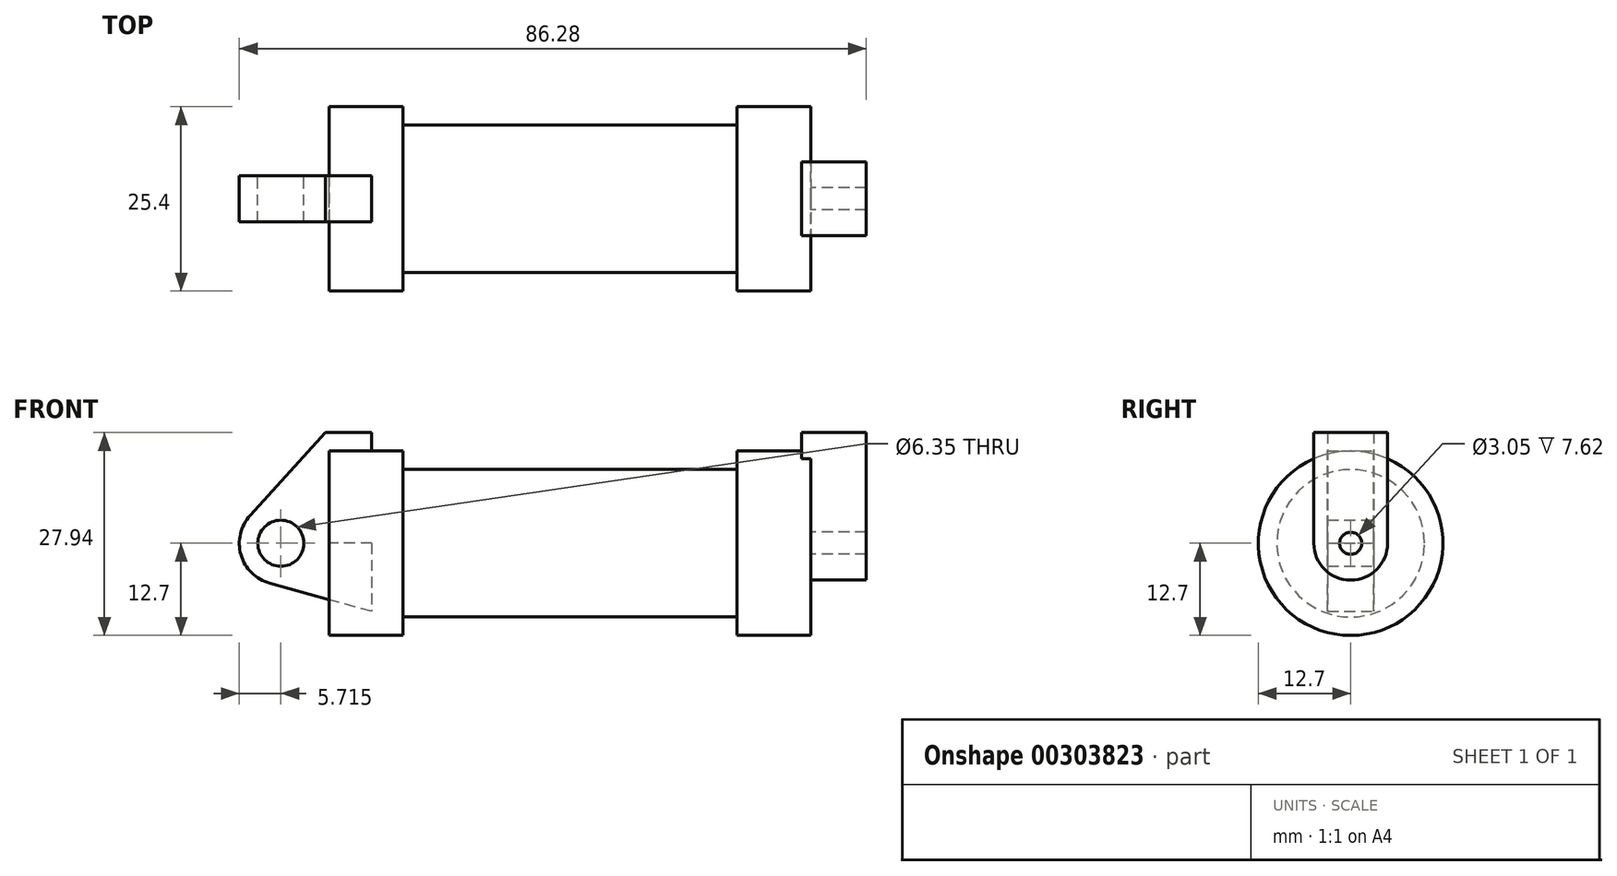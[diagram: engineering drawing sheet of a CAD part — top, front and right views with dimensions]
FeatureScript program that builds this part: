
annotation { "Feature Type Name" : "Feature", "Feature Type Description" : "" }
export const myFeature = defineFeature(function(context is Context, id is Id, definition is map)
    precondition{}
    {
        {
            var Q0;
            Q0=qCreatedBy(makeId("Front.planeOp"),FACE);
            var sketch = newSketch(context, id + "F0", { "sketchPlane" : qUnion([Q0])});
            skLineSegment(sketch, "E0", {"start": v(0, 0) * mm, "end": v(0, 12.7) * mm});
            skLineSegment(sketch, "E1", {"start": v(0, 12.7) * mm, "end": v(10.16, 12.7) * mm});
            skLineSegment(sketch, "E2", {"start": v(10.16, 12.7) * mm, "end": v(10.16, 10.16) * mm});
            skLineSegment(sketch, "E3", {"start": v(10.16, 10.16) * mm, "end": v(56.13, 10.16) * mm});
            skLineSegment(sketch, "E4", {"start": v(56.13, 10.16) * mm, "end": v(56.13, 12.7) * mm});
            skLineSegment(sketch, "E5", {"start": v(56.13, 12.7) * mm, "end": v(66.3, 12.7) * mm});
            skLineSegment(sketch, "E6", {"start": v(66.3, 12.7) * mm, "end": v(66.3, 0) * mm});
            skLineSegment(sketch, "E7", {"start": v(66.3, 0) * mm, "end": v(0, 0) * mm});
            skLineSegment(sketch, "E8", {"start": v(5.84, 15.24) * mm, "end": v(-0.5, 15.24) * mm});
            skLineSegment(sketch, "E9", {"start": v(-0.5, 15.24) * mm, "end": v(-10.88, 3.85) * mm});
            skLineSegment(sketch, "E10", {"start": v(0, 0) * mm, "end": v(-6.65, 0) * mm});
            skCircle(sketch, "E11", {"center": v(-6.65, 0) * mm, "radius": 5.72 * mm});
            skCircle(sketch, "E12", {"center": v(-6.65, 0) * mm, "radius": 3.18 * mm});
            skLineSegment(sketch, "E13", {"start": v(5.84, 15.24) * mm, "end": v(5.84, -9.4) * mm});
            skLineSegment(sketch, "E14", {"start": v(5.84, -9.4) * mm, "end": v(-8.18, -5.5) * mm});
            skSolve(sketch);
        }
        {
            var Q0;
            {var subQ1=sQuery(id+"F0.wireOp",EDGE,"E0");Q0=makeQuery(id+"F0.imprint","IMPRINT",FACE,{"disambiguationData":[TD([[makeQuery(id+"F0.imprint","IMPRINT",EDGE,{"derivedFrom":subQ1}),1.0]])]});}
            var Q1;
            {var subQ0=sQuery(id+"F0.wireOp",EDGE,"E14");Q1=makeQuery(id+"F0.imprint","IMPRINT",FACE,{"disambiguationData":[TD([[makeQuery(id+"F0.imprint","IMPRINT",EDGE,{"derivedFrom":subQ0}),-1.0]])]});}
            var Q2;
            {var subQ5=sQuery(id+"F0.wireOp",EDGE,"E12");Q2=makeQuery(id+"F0.imprint","IMPRINT",FACE,{"disambiguationData":[TD([[makeQuery(id+"F0.imprint","IMPRINT",EDGE,{"derivedFrom":subQ5}),-1.0]])]});}
            extrude(context, id + "F1", {"entities" : qUnion([Q0, Q1, Q2]), "endBound" : BoundingType.SYMMETRIC, "depth" : 6.35 * mm});
        }
        {
            var Q0;
            {var subQ0=sQuery(id+"F0.wireOp",EDGE,"E0");Q0=makeQuery(id+"F0.imprint","IMPRINT",FACE,{"disambiguationData":[TD([[makeQuery(id+"F0.imprint","IMPRINT",EDGE,{"derivedFrom":subQ0}),-1.0]])]});}
            var Q1;
            {var subQ0=sQuery(id+"F0.wireOp",EDGE,"E2");Q1=makeQuery(id+"F0.imprint","IMPRINT",FACE,{"disambiguationData":[TD([[makeQuery(id+"F0.imprint","IMPRINT",EDGE,{"derivedFrom":subQ0}),-1.0]])]});}
            var Q2;
            Q2=sQuery(id+"F0.wireOp",EDGE,"E7");
            revolve(context, id + "F2", {"entities" : qUnion([Q0, Q1]), "axis" : qUnion([Q2]), "revolveType" : RevolveType.FULL});
        }
        {
            var Q0;
            Q0=makeQuery(id+"F2.opRevolve","SWEPT_FACE",FACE,{"disambiguationData":[OSD([sQuery(id+"F0.wireOp",EDGE,"E6")])]});
            var sketch = newSketch(context, id + "F3", { "sketchPlane" : qUnion([Q0])});
            skCircle(sketch, "E15", {"center": v(0, 0) * mm, "radius": 5.08 * mm});
            skCircle(sketch, "E16", {"center": v(0, 0) * mm, "radius": 1.52 * mm});
            skLineSegment(sketch, "E17", {"start": v(-5.08, 0) * mm, "end": v(5.08, 0) * mm, "construction": true});
            skLineSegment(sketch, "E18", {"start": v(-5.08, 0) * mm, "end": v(-5.08, 15.24) * mm});
            skLineSegment(sketch, "E19", {"start": v(-5.08, 15.24) * mm, "end": v(5.08, 15.24) * mm});
            skLineSegment(sketch, "E20", {"start": v(5.08, 15.24) * mm, "end": v(5.08, 0) * mm});
            skSolve(sketch);
        }
        {
            var Q0;
            Q0=makeQuery(id+"F3.imprint","IMPRINT",FACE,{"disambiguationData":[TD([[makeQuery(id+"F3.imprint","IMPRINT",EDGE,{"derivedFrom":sQuery(id+"F3.wireOp",EDGE,"E16")}),-1.0]])]});
            var Q1;
            {var subQ0=sQuery(id+"F3.wireOp",EDGE,"E18");var subQ1=sQuery(id+"F3.wireOp",EDGE,"E15");var subQ2=makeQuery(id+"F3.imprint","INTERSECT",VERTEX,{"derivedFrom":[subQ1,subQ0]});Q1=makeQuery(id+"F3.imprint","IMPRINT",FACE,{"disambiguationData":[TD([[makeQuery(id+"F3.imprint","IMPRINT",EDGE,{"disambiguationData":[TD([[subQ2,1.0]])],"derivedFrom":subQ1}),-1.0]])]});}
            var Q2;
            {var subQ0=sQuery(id+"F3.wireOp",EDGE,"E19");Q2=makeQuery(id+"F3.imprint","IMPRINT",FACE,{"disambiguationData":[TD([[makeQuery(id+"F3.imprint","IMPRINT",EDGE,{"derivedFrom":subQ0}),-1.0]])]});}
            extrude(context, id + "F4", {"entities" : qUnion([Q0, Q1, Q2]), "operationType" : NewBodyOperationType.ADD, "depth" : 7.62 * mm, "hasSecondDirection" : true, "secondDirectionOppositeDirection" : true, "secondDirectionDepth" : 1.27 * mm});
        }
    });
